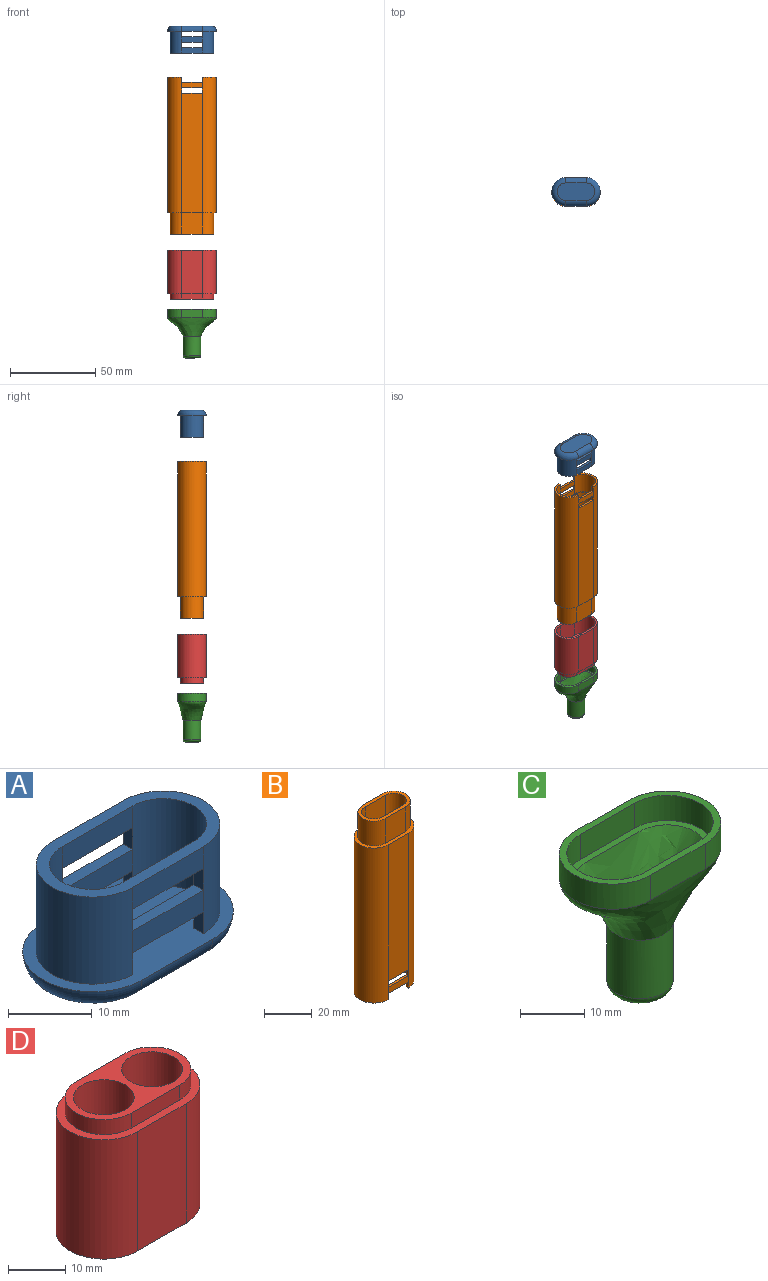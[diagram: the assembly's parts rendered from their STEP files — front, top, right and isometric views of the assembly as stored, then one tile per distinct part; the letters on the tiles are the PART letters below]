
ASSEMBLY  parts=4 mates=3
PART A: 33 faces, bbox 29.9x18x15.9 mm
  f0: plane 11.9x3.18mm, normal (0,-1,0), area 37.8mm2, adj f9,f11,f21,f23
  f1: plane 11.9x3.18mm, normal (0,-1,0), area 37.8mm2, adj f7,f8,f12,f29
  f2: plane 11.9x3.18mm, normal (0,-1,0), area 37.8mm2, adj f7,f8,f26,f31
  f3: plane 11.9x3.18mm, normal (0,1,0), area 37.8mm2, adj f9,f11,f12,f29
  f4: plane 11.9x3.18mm, normal (0,1,0), area 37.8mm2, adj f9,f11,f26,f31
  f5: plane 11.9x3.18mm, normal (0,1,0), area 37.8mm2, adj f7,f8,f12,f25
  f6: plane 11.9x3.18mm, normal (0,1,0), area 37.8mm2, adj f7,f8,f21,f23
  f7: cylinder r=5.16mm len=12.7mm, axis (0,0,-1), area 205.7mm2, adj f1,f2,f5,f6,f12,f13,f20,f24
  f8: cylinder r=5.16mm len=12.7mm, axis (0,0,-1), area 205.7mm2, adj f1,f2,f5,f6,f12,f13,f19,f22
  f9: cylinder r=6.74mm len=13.49mm, axis (0,0,-1), area 269.1mm2, adj f0,f3,f4,f10,f12,f13,f20,f24
  f10: plane 11.9x3.18mm, normal (0,-1,0), area 37.8mm2, adj f9,f11,f12,f25
  f11: cylinder r=6.74mm len=13.49mm, axis (0,0,-1), area 269.1mm2, adj f0,f3,f4,f10,f12,f13,f19,f22
  f12: plane 25.39x13.49mm, normal (0,0,1), area 97.1mm2, adj f1,f3,f5,f7,f8,f9,f10,f11
  f13: plane 28.56x16.66mm, normal (0,0,1), area 357mm2, adj f7,f8,f9,f11,f15,f16,f17,f18
  f14: plane 22.21x10.31mm, normal (0,0,-1), area 206.2mm2, adj f15,f16,f17,f18
  f15: cylinder r=3.17mm len=11.9mm, axis (1,0,0), area 59.3mm2, adj f13,f14,f16,f17
  f16: torus R=5.16mm, axis (0,0,1), area 112.5mm2, adj f13,f14,f15,f18
  f17: torus R=5.16mm, axis (0,0,1), area 112.5mm2, adj f13,f14,f15,f18
  f18: cylinder r=3.17mm len=11.9mm, axis (-1,0,0), area 59.3mm2, adj f13,f14,f16,f17
  f19: plane 3.18x1.59mm, normal (-1,0,0), area 5mm2, adj f8,f11,f13,f21
  f20: plane 3.18x1.59mm, normal (1,0,0), area 5mm2, adj f7,f9,f13,f21
  f21: plane 11.9x1.59mm, normal (0,0,-1), area 18.9mm2, adj f0,f6,f19,f20
  f22: plane 3.18x1.59mm, normal (-1,0,0), area 5mm2, adj f8,f11,f23,f25
  f23: plane 11.9x1.59mm, normal (0,0,1), area 18.9mm2, adj f0,f6,f22,f24
  f24: plane 3.18x1.59mm, normal (1,0,0), area 5mm2, adj f7,f9,f23,f25
  f25: plane 11.9x1.59mm, normal (0,0,-1), area 18.9mm2, adj f5,f10,f22,f24
  f26: plane 11.9x1.59mm, normal (0,0,-1), area 18.9mm2, adj f2,f4,f27,f28
  f27: plane 3.18x1.59mm, normal (-1,0,0), area 5mm2, adj f8,f11,f13,f26
  f28: plane 3.18x1.59mm, normal (1,0,0), area 5mm2, adj f7,f9,f13,f26
  f29: plane 11.9x1.59mm, normal (0,0,-1), area 18.9mm2, adj f1,f3,f30,f32
  f30: plane 3.18x1.59mm, normal (1,0,0), area 5mm2, adj f7,f9,f29,f31
  f31: plane 11.9x1.59mm, normal (0,0,1), area 18.9mm2, adj f2,f4,f30,f32
  f32: plane 3.18x1.59mm, normal (-1,0,0), area 5mm2, adj f8,f11,f29,f31
PART B: 44 faces, bbox 28.6x16.7x92.1 mm
  f0: plane 63.5x11.9mm, normal (0,1,0), area 755.6mm2, adj f1,f3,f19,f43
  f1: cylinder r=6.74mm len=63.5mm, axis (0,0,-1), area 1345.3mm2, adj f0,f2,f19,f43
  f2: plane 63.5x11.9mm, normal (0,-1,0), area 755.6mm2, adj f1,f3,f19,f43
  f3: cylinder r=6.74mm len=63.5mm, axis (0,0,-1), area 1345.3mm2, adj f0,f2,f19,f43
  f4: plane 11.9x3.18mm, normal (0,-1,0), area 37.8mm2, adj f14,f15,f22,f30
  f5: plane 16.66x8.33mm, normal (0,0,-1), area 28.9mm2, adj f14,f17,f28,f31
  f6: plane 11.9x3.18mm, normal (0,1,0), area 37.8mm2, adj f14,f15,f26,f32
  f7: plane 69.85x11.9mm, normal (0,1,0), area 831.2mm2, adj f14,f15,f16,f25
  f8: plane 11.9x3.18mm, normal (0,1,0), area 37.8mm2, adj f17,f18,f22,f30
  f9: plane 11.9x3.18mm, normal (0,1,0), area 37.8mm2, adj f17,f18,f19,f23
  f10: plane 11.9x3.18mm, normal (0,-1,0), area 37.8mm2, adj f17,f18,f26,f32
  f11: plane 11.9x3.18mm, normal (0,-1,0), area 37.8mm2, adj f17,f18,f19,f25
  f12: plane 16.66x8.33mm, normal (0,0,-1), area 28.9mm2, adj f15,f18,f29,f33
  f13: plane 69.85x11.9mm, normal (0,-1,0), area 831.2mm2, adj f14,f15,f16,f23
  f14: cylinder r=8.33mm len=79.38mm, axis (0,0,-1), area 2077.5mm2, adj f4,f5,f6,f7,f13,f16,f20,f24
  f15: cylinder r=8.33mm len=79.38mm, axis (0,0,-1), area 2077.5mm2, adj f4,f6,f7,f12,f13,f16,f21,f27
  f16: plane 28.56x16.66mm, normal (0,0,1), area 113mm2, adj f7,f13,f14,f15,f37,f38,f39,f40
  f17: cylinder r=7.14mm len=14.28mm, axis (0,0,-1), area 284.9mm2, adj f5,f8,f9,f10,f11,f19,f20,f24
  f18: cylinder r=7.14mm len=14.28mm, axis (0,0,-1), area 284.9mm2, adj f8,f9,f10,f11,f12,f19,f21,f27
  f19: plane 26.18x14.28mm, normal (0,0,-1), area 26.8mm2, adj f0,f1,f2,f3,f9,f11,f17,f18
  f20: plane 3.18x1.19mm, normal (1,0,0), area 3.8mm2, adj f14,f17,f22,f23
  f21: plane 3.18x1.19mm, normal (-1,0,0), area 3.8mm2, adj f15,f18,f22,f23
  f22: plane 11.9x1.19mm, normal (0,0,1), area 14.2mm2, adj f4,f8,f20,f21
  f23: plane 11.9x1.19mm, normal (0,0,-1), area 14.2mm2, adj f9,f13,f20,f21
  f24: plane 3.18x1.19mm, normal (1,0,0), area 3.8mm2, adj f14,f17,f25,f26
  f25: plane 11.9x1.19mm, normal (0,0,-1), area 14.2mm2, adj f7,f11,f24,f27
  f26: plane 11.9x1.19mm, normal (0,0,1), area 14.2mm2, adj f6,f10,f24,f27
  f27: plane 3.18x1.19mm, normal (-1,0,0), area 3.8mm2, adj f15,f18,f25,f26
  f28: plane 3.18x1.19mm, normal (1,0,0), area 3.8mm2, adj f5,f14,f17,f30
  f29: plane 3.18x1.19mm, normal (-1,0,0), area 3.8mm2, adj f12,f15,f18,f30
  f30: plane 11.9x1.19mm, normal (0,0,-1), area 14.2mm2, adj f4,f8,f28,f29
  f31: plane 3.18x1.19mm, normal (1,0,0), area 3.8mm2, adj f5,f14,f17,f32
  f32: plane 11.9x1.19mm, normal (0,0,-1), area 14.2mm2, adj f6,f10,f31,f33
  f33: plane 3.18x1.19mm, normal (-1,0,0), area 3.8mm2, adj f12,f15,f18,f32
  f34: cylinder r=5.16mm len=15.88mm, axis (0,0,-1), area 257.2mm2, adj f35,f41,f42,f43
  f35: plane 15.88x11.9mm, normal (0,-1,0), area 188.9mm2, adj f34,f36,f42,f43
  f36: cylinder r=5.16mm len=15.88mm, axis (0,0,-1), area 257.2mm2, adj f35,f41,f42,f43
  f37: cylinder r=6.74mm len=13.49mm, axis (0,0,-1), area 269.1mm2, adj f16,f38,f40,f42
  f38: plane 12.7x11.9mm, normal (0,-1,0), area 151.1mm2, adj f16,f37,f39,f42
  f39: cylinder r=6.74mm len=13.49mm, axis (0,0,-1), area 269.1mm2, adj f16,f38,f40,f42
  f40: plane 12.7x11.9mm, normal (0,1,0), area 151.1mm2, adj f16,f37,f39,f42
  f41: plane 15.88x11.9mm, normal (0,1,0), area 188.9mm2, adj f34,f36,f42,f43
  f42: plane 25.39x13.49mm, normal (0,0,1), area 97.1mm2, adj f34,f35,f36,f37,f38,f39,f40,f41
  f43: plane 25.39x13.49mm, normal (0,0,-1), area 97.1mm2, adj f0,f1,f2,f3,f34,f35,f36,f41
PART C: 15 faces, bbox 28.9x17x29 mm
  f0: plane 11.96x4.82mm, normal (0,1,0), area 56.7mm2, adj f1,f3,f10,f14
  f1: cylinder r=8.33mm len=16.66mm, axis (0,0,-1), area 124.7mm2, adj f0,f2,f10,f14
  f2: plane 11.96x4.82mm, normal (0,-1,0), area 56.7mm2, adj f1,f3,f10,f14
  f3: cylinder r=8.33mm len=16.66mm, axis (0,0,-1), area 124.7mm2, adj f0,f2,f10,f14
  f4: plane 11.9x4.76mm, normal (0,-1,0), area 56.7mm2, adj f5,f7,f13,f14
  f5: cylinder r=7.14mm len=14.28mm, axis (0,0,1), area 106.8mm2, adj f4,f6,f13,f14
  f6: plane 11.9x4.76mm, normal (0,1,0), area 56.7mm2, adj f5,f7,f13,f14
  f7: cylinder r=7.14mm len=14.28mm, axis (0,0,1), area 106.8mm2, adj f4,f6,f13,f14
  f8: cylinder r=3.57mm len=12.7mm, axis (0,0,1), area 284.8mm2, adj f11,f12
  f9: cylinder r=5.16mm len=11.11mm, axis (0,0,1), area 360mm2, adj f10,f12
  f10: bspline ~28.52x16.66mm, area 689.4mm2, adj f0,f1,f2,f3,f9
  f11: bspline ~23.78x11.9mm, area 510.8mm2, adj f8,f13
  f12: torus R=3.57mm, axis (0,0,-1), area 71.7mm2, adj f8,f9
  f13: plane 26.57x14.67mm, normal (0,0,1), area 77.3mm2, adj f4,f5,f6,f7,f11
  f14: plane 28.56x16.66mm, normal (0,0,1), area 86.2mm2, adj f0,f1,f2,f3,f4,f5,f6,f7
PART D: 18 faces, bbox 28.6x16.7x28.6 mm
  f0: plane 26.18x14.28mm, normal (0,0,-1), area 154.7mm2, adj f4,f6,f13,f14,f15,f16
  f1: plane 11.9x3.18mm, normal (0,1,0), area 37.8mm2, adj f2,f5,f7,f12
  f2: cylinder r=6.74mm len=13.49mm, axis (0,0,-1), area 67.3mm2, adj f1,f3,f7,f12
  f3: plane 11.9x3.18mm, normal (0,-1,0), area 37.8mm2, adj f2,f5,f7,f12
  f4: cylinder r=5.28mm len=15.88mm, axis (0,0,-1), area 527mm2, adj f0,f7
  f5: cylinder r=6.74mm len=13.49mm, axis (0,0,-1), area 67.3mm2, adj f1,f3,f7,f12
  f6: cylinder r=5.28mm len=15.88mm, axis (0,0,-1), area 527mm2, adj f0,f7
  f7: plane 25.39x13.49mm, normal (0,0,1), area 128mm2, adj f1,f2,f3,f4,f5,f6
  f8: plane 25.4x11.9mm, normal (0,1,0), area 302.3mm2, adj f9,f11,f12,f17
  f9: cylinder r=8.33mm len=25.4mm, axis (0,0,-1), area 664.8mm2, adj f8,f10,f12,f17
  f10: plane 25.4x11.9mm, normal (0,-1,0), area 302.3mm2, adj f9,f11,f12,f17
  f11: cylinder r=8.33mm len=25.4mm, axis (0,0,-1), area 664.8mm2, adj f8,f10,f12,f17
  f12: plane 28.56x16.66mm, normal (0,0,1), area 113mm2, adj f1,f2,f3,f5,f8,f9,f10,f11
  f13: plane 12.7x11.9mm, normal (0,1,0), area 151.1mm2, adj f0,f14,f16,f17
  f14: cylinder r=7.14mm len=14.28mm, axis (0,0,1), area 284.9mm2, adj f0,f13,f15,f17
  f15: plane 12.7x11.9mm, normal (0,-1,0), area 151.1mm2, adj f0,f14,f16,f17
  f16: cylinder r=7.14mm len=14.28mm, axis (0,0,1), area 284.9mm2, adj f0,f13,f15,f17
  f17: plane 28.56x16.66mm, normal (0,0,-1), area 86.2mm2, adj f8,f9,f10,f11,f13,f14,f15,f16
PLACE A rot(axis=(0,1,0),180deg) t=(-111.39,80.62,61.5)mm
PLACE B rot(axis=(1,0,0),180deg) t=(-117.34,80.62,-44.62)mm
PLACE C rot(axis=(0.99,0,0.11),0deg) t=(-117.34,80.62,-104.42)mm
PLACE D rot(axis=(0,1,0),180deg) t=(-111.39,80.62,-79.41)mm
MATE slider B.f16 <-> D.f17  axis (0,0,-1) through (-111.39,80.62,-44.62)mm
MATE slider C.f8 <-> B.f16  axis (0,0,1) through (-111.39,80.62,-101.25)mm
MATE slider B.f3 <-> A.f17  axis (0,0,1) through (-105.44,80.62,34.76)mm
